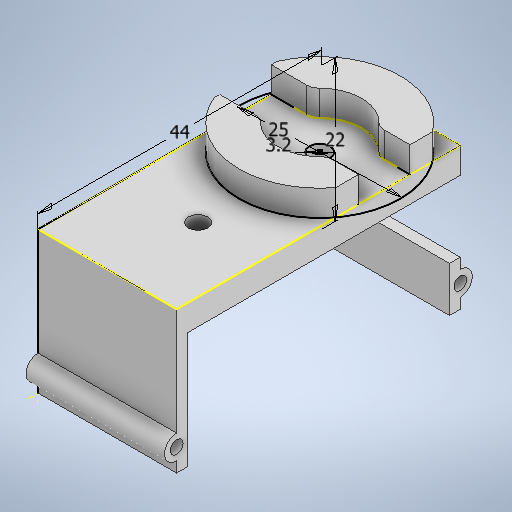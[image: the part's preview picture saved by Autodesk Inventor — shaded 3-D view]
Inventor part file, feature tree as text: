
AUTODESK INVENTOR PART (.ipt)
format: ipt  version: 2025.2 (Build 292293000, 293)  size: 785,408 bytes
history: native  units: in
note: dims shown in document units (in); Inventor stores cm internally (conversion verified against a paired STEP export)
features: extrude x11, sketch x11, projected_geometry x10, fillet x1
ambient origin geometry x8: Origin, YZ Plane, XZ Plane, XY Plane, X Axis, Y Axis, Z Axis, Center Point
bodies: Solid1 (feature_tree)
feature tree (33):
  extrude  "Extrusion1"  Depth=0.7874in
  sketch  "Sketch2"  dims[d2=0.9055in d3=1.7323in]
  extrude  "Extrusion2"  Depth=1.7323in
  extrude  "Extrusion3"  Depth=1.7323in
  extrude  "Extrusion4"  Depth=0.4331in TaperAngle=0.0deg
  fillet  "Fillet1"  Radius=0.1575in
  sketch  "Sketch6"  dims[d14=0.7087in d15=0.1575in]
  extrude  "Extrusion5"  Depth=0.5118in
  extrude  "Extrusion6"  Depth=0.1575in
  extrude  "Extrusion7"  Depth=0.1575in TaperAngle=0.0deg
  extrude  "Extrusion8"  Depth=0.0787in
  extrude  "Extrusion9"  Depth=0.3937in TaperAngle=0.0deg
  extrude  "Extrusion10"  Depth=0.3937in
  extrude  "Extrusion11"  Depth=0.3937in TaperAngle=0.0deg
  sketch  "Sketch1"  dims[d0=0.7874in d1=1.5846in]
  sketch  "Sketch3"  dims[d4=0.2756in d5=0.0in d6=1.7323in]
  projected_geometry  "Projected Loop1"
  sketch  "Sketch4"  dims[d7=0.8661in d8=0.4331in d9=0.0in d10=0.1575in d11=0.0in]
  sketch  "Sketch5"  dims[d12=0.4646in d13=0.5118in]
  projected_geometry  "Projected Loop2"
  projected_geometry  "Projected Loop3"
  projected_geometry  "Projected Loop4"
  projected_geometry  "Projected Loop5"
  sketch  "Sketch7"  dims[d16=0.1575in d17=0.1575in d18=0.0in]
  projected_geometry  "Projected Loop6"
  projected_geometry  "Projected Loop7"
  sketch  "Sketch8"  dims[d19=0.0787in d20=0.9843in]
  projected_geometry  "Projected Loop8"
  projected_geometry  "Projected Loop9"
  sketch  "Sketch9"  dims[d21=0.126in d22=0.3937in d23=0.0in]
  sketch  "Sketch10"  dims[d24=0.3937in d25=0.0in d26=0.1476in]
  projected_geometry  "Projected Loop10"
  sketch  "Sketch11"  dims[d27=0.1476in d28=0.3937in d29=0.0in d30=0.0787in d31=0.0787in d32=0.2362in d33=0.0in d34=0.0079in d35=0.0079in d36=0.2362in d37=0.0in d38=0.1969in d39=0.0in d40=0.1181in d41=0.1969in d42=0.0in]
